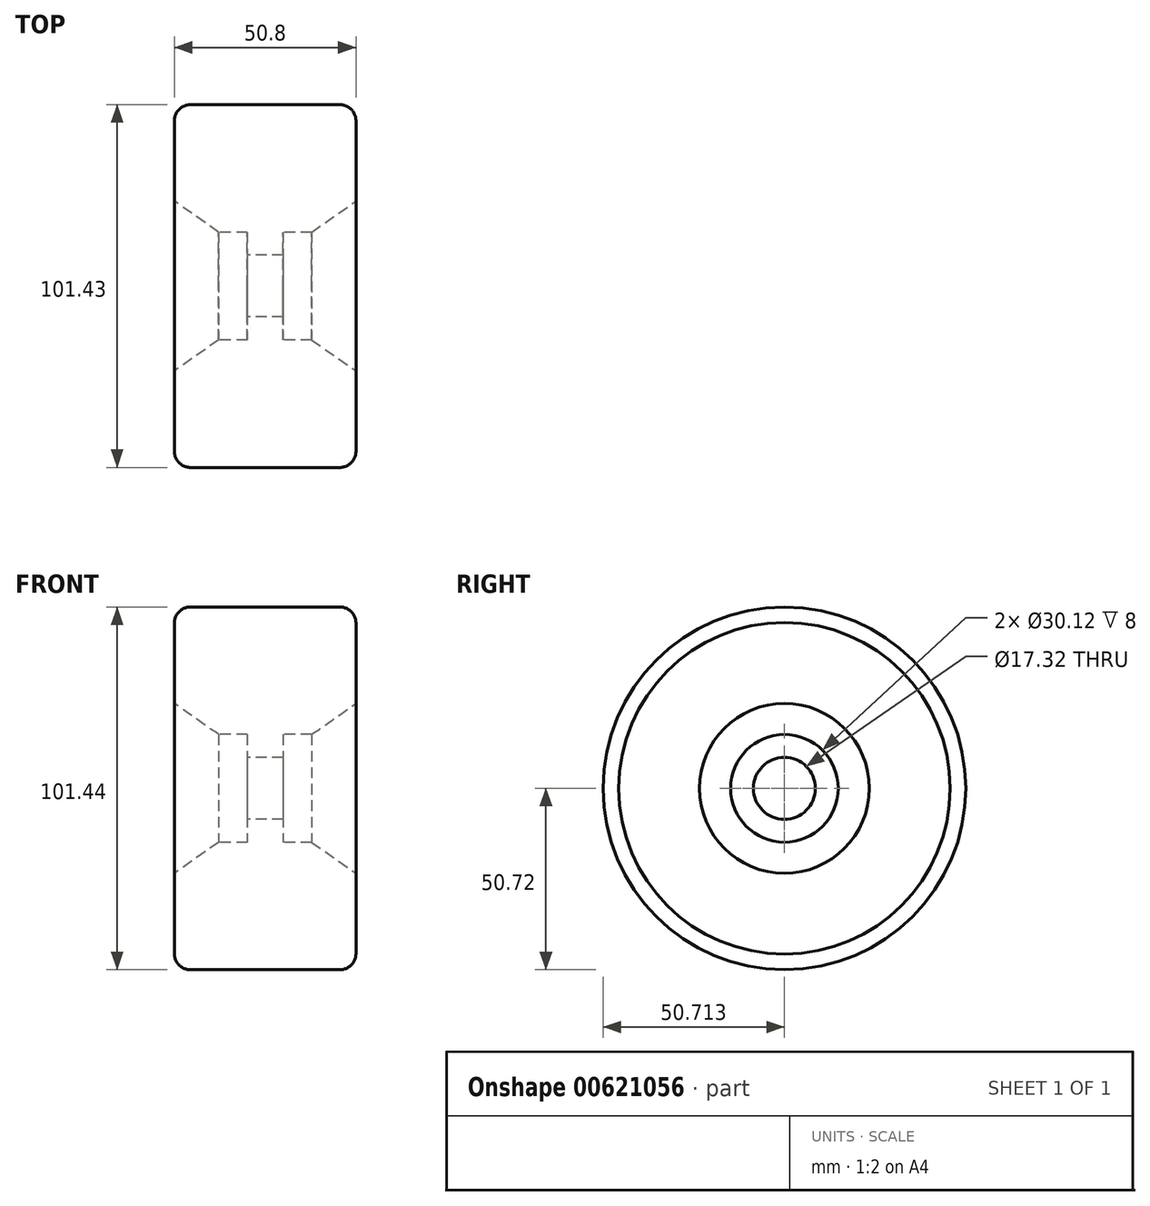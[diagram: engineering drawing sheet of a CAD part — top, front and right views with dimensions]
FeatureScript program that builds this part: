
annotation { "Feature Type Name" : "Feature", "Feature Type Description" : "" }
export const myFeature = defineFeature(function(context is Context, id is Id, definition is map)
    precondition{}
    {
        {
            var Q0;
            Q0=qCreatedBy(makeId("Top.planeOp"),FACE);
            var sketch = newSketch(context, id + "F0", { "sketchPlane" : qUnion([Q0])});
            skLineSegment(sketch, "E0", {"start": v(5, -20.14) * mm, "end": v(5, -17.79) * mm});
            skLineSegment(sketch, "E1", {"start": v(5, -17.79) * mm, "end": v(13, -17.79) * mm});
            skLineSegment(sketch, "E2", {"start": v(13, -17.79) * mm, "end": v(25.4, -9.1) * mm});
            skLineSegment(sketch, "E3", {"start": v(0, 17.87) * mm, "end": v(20.85, 17.87) * mm});
            skLineSegment(sketch, "E4", {"start": v(25.4, 13.5) * mm, "end": v(25.4, -9.1) * mm});
            skArc(sketch, "E5", {"start": v(25.4, 13.5) * mm, "mid": v(24, 16.6) * mm, "end": v(20.85, 17.87) * mm});
            skLineSegment(sketch, "E6", {"start": v(-5, -20.14) * mm, "end": v(-5, -17.79) * mm});
            skLineSegment(sketch, "E7", {"start": v(-5, -17.79) * mm, "end": v(-13, -17.79) * mm});
            skLineSegment(sketch, "E8", {"start": v(0, 17.87) * mm, "end": v(-20.85, 17.87) * mm});
            skLineSegment(sketch, "E9", {"start": v(-25.4, 13.5) * mm, "end": v(-25.4, -9.1) * mm});
            skLineSegment(sketch, "E10", {"start": v(-13, -17.79) * mm, "end": v(-25.4, -9.1) * mm});
            skArc(sketch, "E11", {"start": v(-20.85, 17.87) * mm, "mid": v(-24, 16.6) * mm, "end": v(-25.4, 13.5) * mm});
            skLineSegment(sketch, "E12", {"start": v(-5, -20.14) * mm, "end": v(-5, -24.19) * mm});
            skLineSegment(sketch, "E13", {"start": v(-5, -24.19) * mm, "end": v(5, -24.19) * mm});
            skLineSegment(sketch, "E14", {"start": v(5, -20.14) * mm, "end": v(5, -24.19) * mm});
            skLineSegment(sketch, "E15", {"start": v(-17.32, -32.85) * mm, "end": v(21.32, -32.85) * mm});
            skSolve(sketch);
        }
        {
            var Q0;
            Q0 = qSketchRegion(id + "F0", true);
            var Q1;
            Q1=sQuery(id+"F0.wireOp",EDGE,"E15");
            revolve(context, id + "F1", {"entities" : qUnion([Q0]), "axis" : qUnion([Q1]), "revolveType" : RevolveType.FULL});
        }
        {
            var Q0;
            Q0=makeQuery(id+"F1.opRevolve","SWEPT_BODY",BODY,{"disambiguationData":[OSD([sQuery(id+"F0.wireOp",EDGE,"G3Ar4VSh-pd1C-kD4C-DxUM-zFE8SN6wWrOT"),sQuery(id+"F0.wireOp",EDGE,"xW7kevFj-OZBr-E8gR-e2AB-gybxMCRJ84sr"),sQuery(id+"F0.wireOp",EDGE,"E0"),sQuery(id+"F0.wireOp",EDGE,"E1"),sQuery(id+"F0.wireOp",EDGE,"E2"),sQuery(id+"F0.wireOp",EDGE,"E3"),sQuery(id+"F0.wireOp",EDGE,"E4"),sQuery(id+"F0.wireOp",EDGE,"E5")])]});
            var Q1;
            Q1=qCreatedBy(makeId("Top.planeOp"),FACE);
            mirror(context, id + "F2", {"operationType" : NewBodyOperationType.ADD, "entities" : qUnion([Q0]), "mirrorPlane" : qUnion([Q1])});
        }
    });
